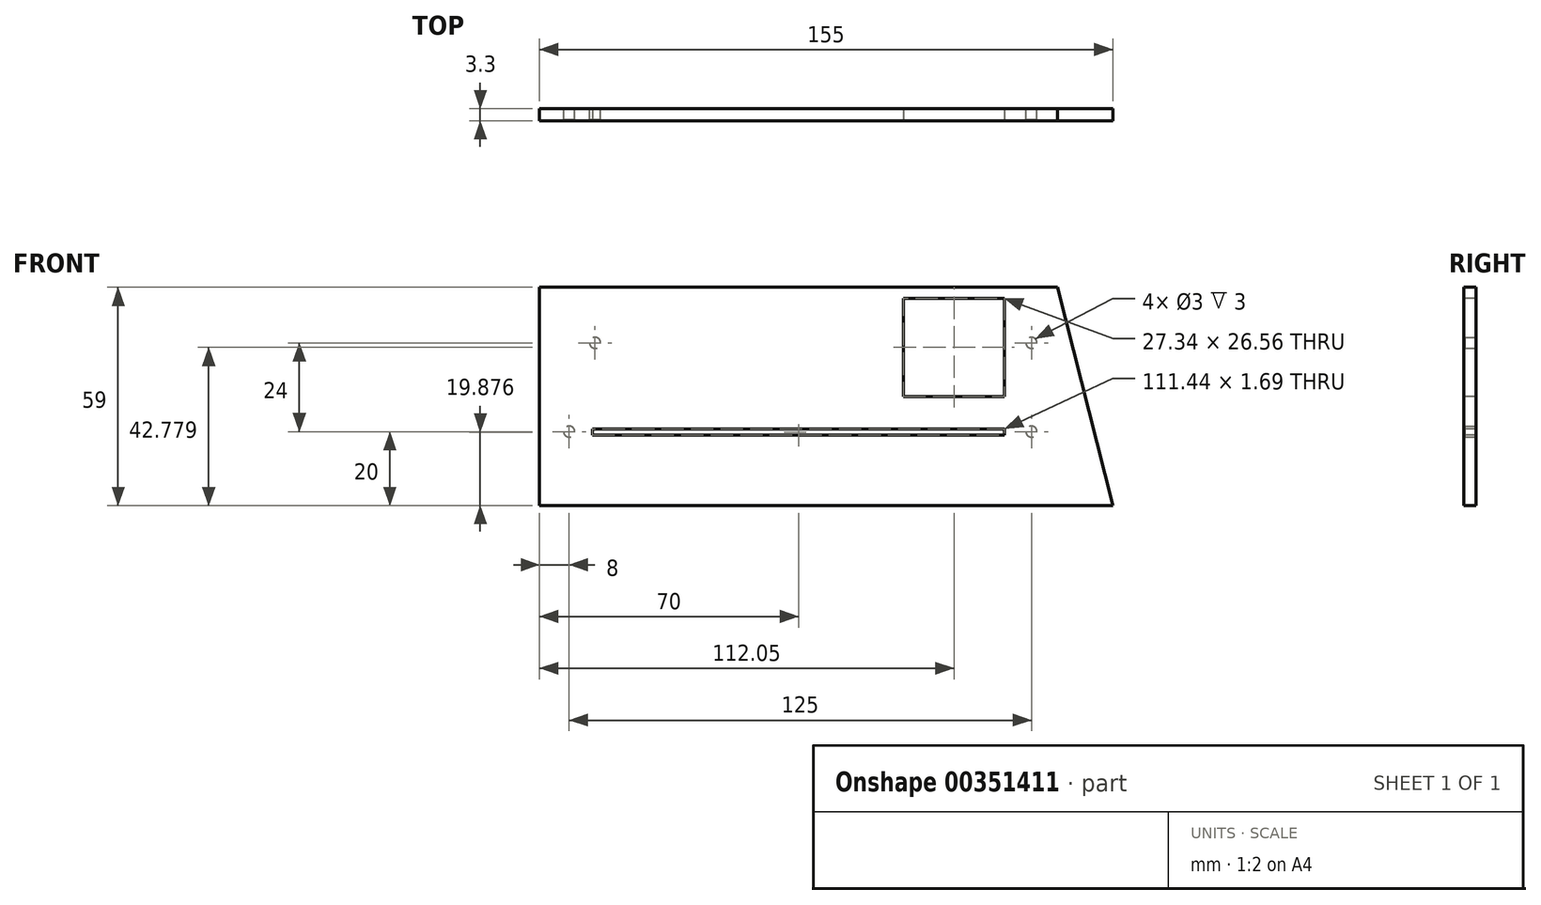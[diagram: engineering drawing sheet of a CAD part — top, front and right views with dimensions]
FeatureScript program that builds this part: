
annotation { "Feature Type Name" : "Feature", "Feature Type Description" : "" }
export const myFeature = defineFeature(function(context is Context, id is Id, definition is map)
    precondition{}
    {
        {
            var Q0;
            Q0=qCreatedBy(makeId("Front.planeOp"),FACE);
            var sketch = newSketch(context, id + "F0", { "sketchPlane" : qUnion([Q0])});
            skLineSegment(sketch, "E0.bottom", {"start": v(70, 29.5) * mm, "end": v(-70, 29.5) * mm});
            skLineSegment(sketch, "E0.top", {"start": v(70, -29.5) * mm, "end": v(-70, -29.5) * mm});
            skLineSegment(sketch, "E0.left", {"start": v(70, 29.5) * mm, "end": v(70, -29.5) * mm});
            skLineSegment(sketch, "E0.right", {"start": v(-70, 29.5) * mm, "end": v(-70, -29.5) * mm});
            skPoint(sketch, "E0.middle", {"position": v(0, 0) * mm});
            skLineSegment(sketch, "E1", {"start": v(70, 29.5) * mm, "end": v(85, -29.5) * mm});
            skLineSegment(sketch, "E2", {"start": v(85, -29.5) * mm, "end": v(70, -29.5) * mm});
            skSolve(sketch);
        }
        {
            var Q0;
            Q0=qSketchRegion(id+"F0",true);
            extrude(context, id + "F1", {"entities" : qUnion([Q0]), "depth" : 3.3 * mm});
        }
        {
            var Q0;
            Q0=makeQuery(id+"F1.opExtrude","CAP_FACE",FACE,{"disambiguationData":[OSD([sQuery(id+"F0.wireOp",EDGE,"E0.bottom"),sQuery(id+"F0.wireOp",EDGE,"E0.top"),sQuery(id+"F0.wireOp",EDGE,"E0.right"),sQuery(id+"F0.wireOp",EDGE,"E1"),sQuery(id+"F0.wireOp",EDGE,"E2")])],"isStart":false});
            var sketch = newSketch(context, id + "F2", { "sketchPlane" : qUnion([Q0])});
            skLineSegment(sketch, "E3.bottom", {"start": v(55.72, -8.78) * mm, "end": v(-55.72, -8.78) * mm});
            skLineSegment(sketch, "E3.top", {"start": v(55.72, -10.47) * mm, "end": v(-55.72, -10.47) * mm});
            skLineSegment(sketch, "E3.left", {"start": v(55.72, -8.78) * mm, "end": v(55.72, -10.47) * mm});
            skLineSegment(sketch, "E3.right", {"start": v(-55.72, -8.78) * mm, "end": v(-55.72, -10.47) * mm});
            skPoint(sketch, "E3.middle", {"position": v(0, -9.62) * mm});
            skSolve(sketch);
        }
        {
            var Q0;
            Q0=qSketchRegion(id+"F2",true);
            extrude(context, id + "F3", {"entities" : qUnion([Q0]), "operationType" : NewBodyOperationType.REMOVE, "oppositeDirection" : true, "depth" : 25 * mm});
        }
        {
            var Q0;
            Q0=makeQuery(id+"F1.opExtrude","CAP_FACE",FACE,{"disambiguationData":[OSD([sQuery(id+"F0.wireOp",EDGE,"E0.bottom"),sQuery(id+"F0.wireOp",EDGE,"E0.top"),sQuery(id+"F0.wireOp",EDGE,"E0.right"),sQuery(id+"F0.wireOp",EDGE,"E1"),sQuery(id+"F0.wireOp",EDGE,"E2")])],"isStart":false});
            var sketch = newSketch(context, id + "F4", { "sketchPlane" : qUnion([Q0])});
            skLineSegment(sketch, "E4.bottom", {"start": v(28.38, 22.22) * mm, "end": v(55.72, 22.22) * mm});
            skLineSegment(sketch, "E4.top", {"start": v(28.38, 3.22) * mm, "end": v(55.72, 3.22) * mm});
            skLineSegment(sketch, "E4.left", {"start": v(28.38, 22.22) * mm, "end": v(28.38, 3.22) * mm});
            skLineSegment(sketch, "E4.right", {"start": v(55.72, 22.22) * mm, "end": v(55.72, 3.22) * mm});
            skSolve(sketch);
        }
        {
            var Q0;
            Q0=qSketchRegion(id+"F4",true);
            extrude(context, id + "F5", {"entities" : qUnion([Q0]), "operationType" : NewBodyOperationType.REMOVE, "oppositeDirection" : true, "depth" : 25 * mm});
        }
        {
            var Q0;
            Q0=makeQuery(id+"F1.opExtrude","CAP_FACE",FACE,{"disambiguationData":[OSD([sQuery(id+"F0.wireOp",EDGE,"E0.bottom"),sQuery(id+"F0.wireOp",EDGE,"E0.top"),sQuery(id+"F0.wireOp",EDGE,"E0.right"),sQuery(id+"F0.wireOp",EDGE,"E1"),sQuery(id+"F0.wireOp",EDGE,"E2")])],"isStart":false});
            var sketch = newSketch(context, id + "F6", { "sketchPlane" : qUnion([Q0])});
            skLineSegment(sketch, "E5.bottom", {"start": v(28.38, 26.56) * mm, "end": v(55.72, 26.56) * mm});
            skLineSegment(sketch, "E5.top", {"start": v(28.38, 0) * mm, "end": v(55.72, 0) * mm});
            skLineSegment(sketch, "E5.left", {"start": v(28.38, 26.56) * mm, "end": v(28.38, 0) * mm});
            skLineSegment(sketch, "E5.right", {"start": v(55.72, 26.56) * mm, "end": v(55.72, 0) * mm});
            skSolve(sketch);
        }
        {
            var Q0;
            Q0=qSketchRegion(id+"F6",true);
            extrude(context, id + "F7", {"entities" : qUnion([Q0]), "operationType" : NewBodyOperationType.REMOVE, "oppositeDirection" : true, "depth" : 25 * mm});
        }
        {
            var Q0;
            Q0=makeQuery(id+"F1.opExtrude","CAP_FACE",FACE,{"disambiguationData":[OSD([sQuery(id+"F0.wireOp",EDGE,"E0.bottom"),sQuery(id+"F0.wireOp",EDGE,"E0.top"),sQuery(id+"F0.wireOp",EDGE,"E0.right"),sQuery(id+"F0.wireOp",EDGE,"E1"),sQuery(id+"F0.wireOp",EDGE,"E2")])],"isStart":true});
            var sketch = newSketch(context, id + "F8", { "sketchPlane" : qUnion([Q0])});
            skCircle(sketch, "E6", {"center": v(55, 14.5) * mm, "radius": 1.5 * mm});
            skCircle(sketch, "E7", {"center": v(62, -9.5) * mm, "radius": 1.5 * mm});
            skCircle(sketch, "E8", {"center": v(-63, -9.5) * mm, "radius": 1.5 * mm});
            skCircle(sketch, "E9", {"center": v(-63, 14.5) * mm, "radius": 1.5 * mm});
            skLineSegment(sketch, "E10", {"start": v(-70, 29.5) * mm, "end": v(-70, -29.5) * mm, "construction": true});
            skSolve(sketch);
        }
        {
            var Q0;
            Q0 = qSketchRegion(id + "F8", true);
            extrude(context, id + "F9", {"entities" : qUnion([Q0]), "operationType" : NewBodyOperationType.REMOVE, "oppositeDirection" : true, "depth" : 3 * mm});
        }
    });
